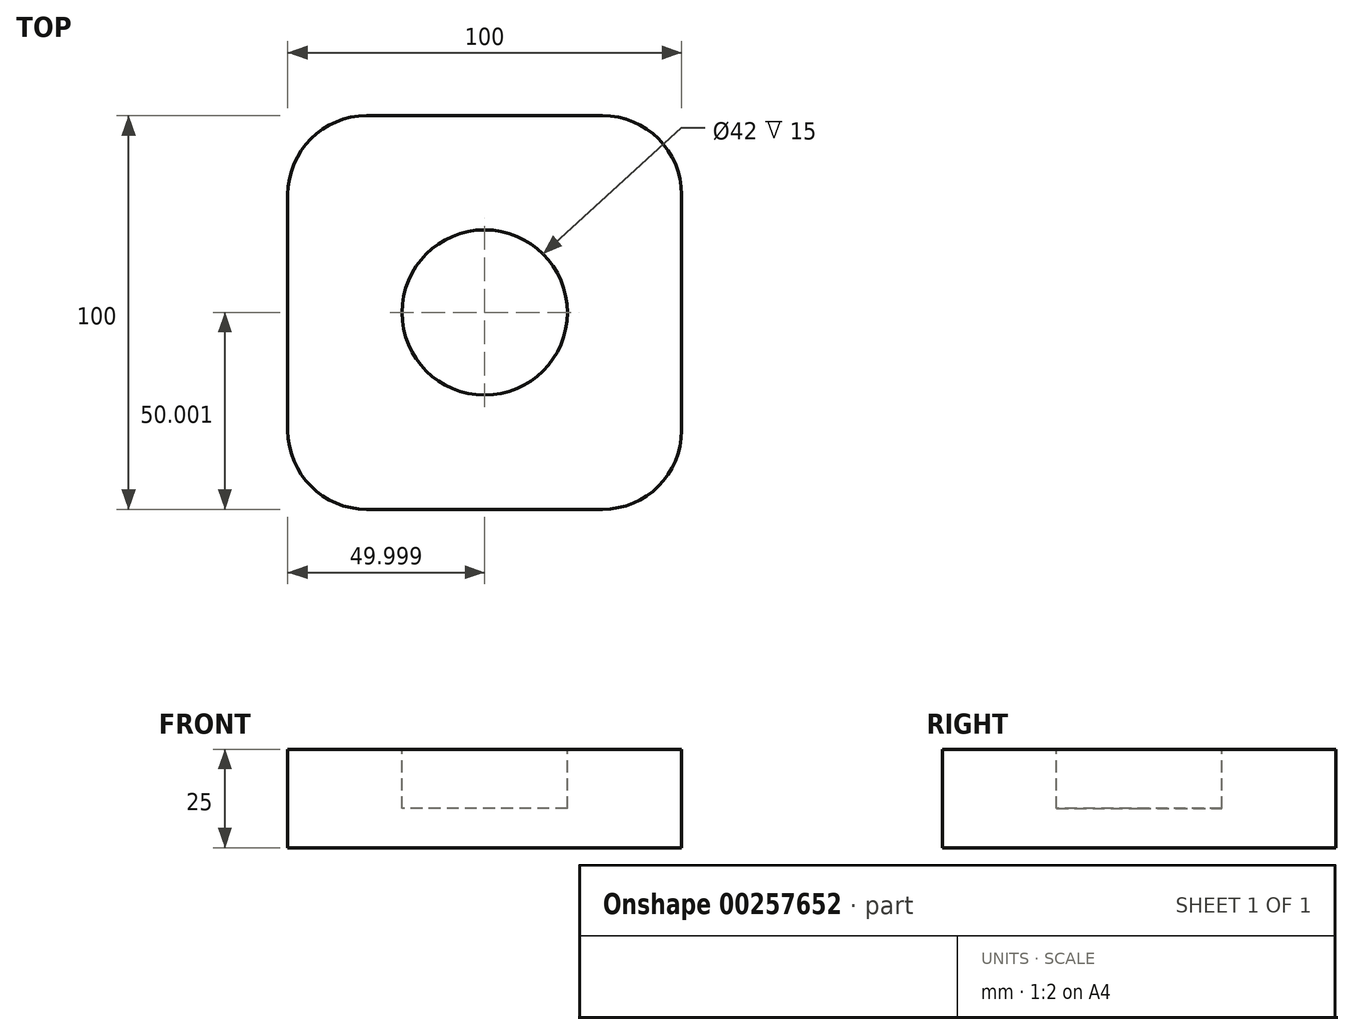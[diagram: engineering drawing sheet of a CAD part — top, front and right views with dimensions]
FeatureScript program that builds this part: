
annotation { "Feature Type Name" : "Feature", "Feature Type Description" : "" }
export const myFeature = defineFeature(function(context is Context, id is Id, definition is map)
    precondition{}
    {
        {
            var Q0;
            Q0=qCreatedBy(makeId("Top.planeOp"),FACE);
            var sketch = newSketch(context, id + "F0", { "sketchPlane" : qUnion([Q0])});
            skLineSegment(sketch, "E0.bottom", {"start": v(-108.56, 72.56) * mm, "end": v(-8.56, 72.56) * mm});
            skLineSegment(sketch, "E0.top", {"start": v(-108.56, -27.44) * mm, "end": v(-8.56, -27.44) * mm});
            skLineSegment(sketch, "E0.left", {"start": v(-108.56, 72.56) * mm, "end": v(-108.56, -27.44) * mm});
            skLineSegment(sketch, "E0.right", {"start": v(-8.56, 72.56) * mm, "end": v(-8.56, -27.44) * mm});
            skLineSegment(sketch, "E1", {"start": v(-108.56, 72.56) * mm, "end": v(-8.56, -27.44) * mm});
            skLineSegment(sketch, "E2", {"start": v(-8.56, 72.56) * mm, "end": v(-108.56, -27.44) * mm});
            skSolve(sketch);
        }
        {
            var Q0;
            {var subQ0=sQuery(id+"F0.wireOp",EDGE,"E0.left");Q0=makeQuery(id+"F0.imprint","IMPRINT",FACE,{"disambiguationData":[TD([[makeQuery(id+"F0.imprint","IMPRINT",EDGE,{"derivedFrom":subQ0}),1.0]])]});}
            var Q1;
            {var subQ0=sQuery(id+"F0.wireOp",EDGE,"E0.bottom");Q1=makeQuery(id+"F0.imprint","IMPRINT",FACE,{"disambiguationData":[TD([[makeQuery(id+"F0.imprint","IMPRINT",EDGE,{"derivedFrom":subQ0}),-1.0]])]});}
            var Q2;
            {var subQ0=sQuery(id+"F0.wireOp",EDGE,"E0.right");Q2=makeQuery(id+"F0.imprint","IMPRINT",FACE,{"disambiguationData":[TD([[makeQuery(id+"F0.imprint","IMPRINT",EDGE,{"derivedFrom":subQ0}),-1.0]])]});}
            var Q3;
            {var subQ0=sQuery(id+"F0.wireOp",EDGE,"E0.top");Q3=makeQuery(id+"F0.imprint","IMPRINT",FACE,{"disambiguationData":[TD([[makeQuery(id+"F0.imprint","IMPRINT",EDGE,{"derivedFrom":subQ0}),1.0]])]});}
            extrude(context, id + "F1", {"entities" : qUnion([Q0, Q1, Q2, Q3]), "depth" : 25 * mm});
        }
        {
            var Q0;
            Q0=makeQuery(id+"F1.opExtrude","CAP_FACE",FACE,{"disambiguationData":[OSD([sQuery(id+"F0.wireOp",EDGE,"E0.bottom"),sQuery(id+"F0.wireOp",EDGE,"E0.top"),sQuery(id+"F0.wireOp",EDGE,"E0.left"),sQuery(id+"F0.wireOp",EDGE,"E0.right")])],"isStart":false});
            var sketch = newSketch(context, id + "F2", { "sketchPlane" : qUnion([Q0])});
            skCircle(sketch, "E3", {"center": v(-58.56, 22.56) * mm, "radius": 21 * mm});
            skPoint(sketch, "E3.centerSnap0", {"position": v(-8.56, 22.56) * mm});
            skPoint(sketch, "E3.centerSnap1", {"position": v(-58.56, -27.44) * mm});
            skSolve(sketch);
        }
        {
            var Q0;
            Q0 = qSketchRegion(id + "F2", true);
            extrude(context, id + "F3", {"entities" : qUnion([Q0]), "operationType" : NewBodyOperationType.REMOVE, "oppositeDirection" : true, "depth" : 15 * mm});
        }
        {
            var Q0;
            Q0=makeQuery(id+"F1.opExtrude","SWEPT_EDGE",EDGE,{"disambiguationData":[OSD([sQuery(id+"F0.wireOp",EDGE,"E0.top"),sQuery(id+"F0.wireOp",EDGE,"E0.left"),sQuery(id+"F0.wireOp",EDGE,"E2")])]});
            fillet(context, id + "F4", {"entities" : qUnion([Q0]), "radius" : 20 * mm, "tangentPropagation" : true, "allowEdgeOverflow" : false});
        }
        {
            var Q0;
            Q0=makeQuery(id+"F1.opExtrude","SWEPT_EDGE",EDGE,{"disambiguationData":[OSD([sQuery(id+"F0.wireOp",EDGE,"E0.bottom"),sQuery(id+"F0.wireOp",EDGE,"E0.left"),sQuery(id+"F0.wireOp",EDGE,"E1")])]});
            fillet(context, id + "F5", {"entities" : qUnion([Q0]), "radius" : 20 * mm, "tangentPropagation" : true, "allowEdgeOverflow" : false});
        }
        {
            var Q0;
            Q0=makeQuery(id+"F1.opExtrude","SWEPT_EDGE",EDGE,{"disambiguationData":[OSD([sQuery(id+"F0.wireOp",EDGE,"E0.bottom"),sQuery(id+"F0.wireOp",EDGE,"E0.right"),sQuery(id+"F0.wireOp",EDGE,"E2")])]});
            var Q1;
            Q1=makeQuery(id+"F1.opExtrude","SWEPT_EDGE",EDGE,{"disambiguationData":[OSD([sQuery(id+"F0.wireOp",EDGE,"E0.top"),sQuery(id+"F0.wireOp",EDGE,"E0.right"),sQuery(id+"F0.wireOp",EDGE,"E1")])]});
            fillet(context, id + "F6", {"entities" : qUnion([Q0, Q1]), "radius" : 20 * mm, "tangentPropagation" : true, "allowEdgeOverflow" : false});
        }
    });
